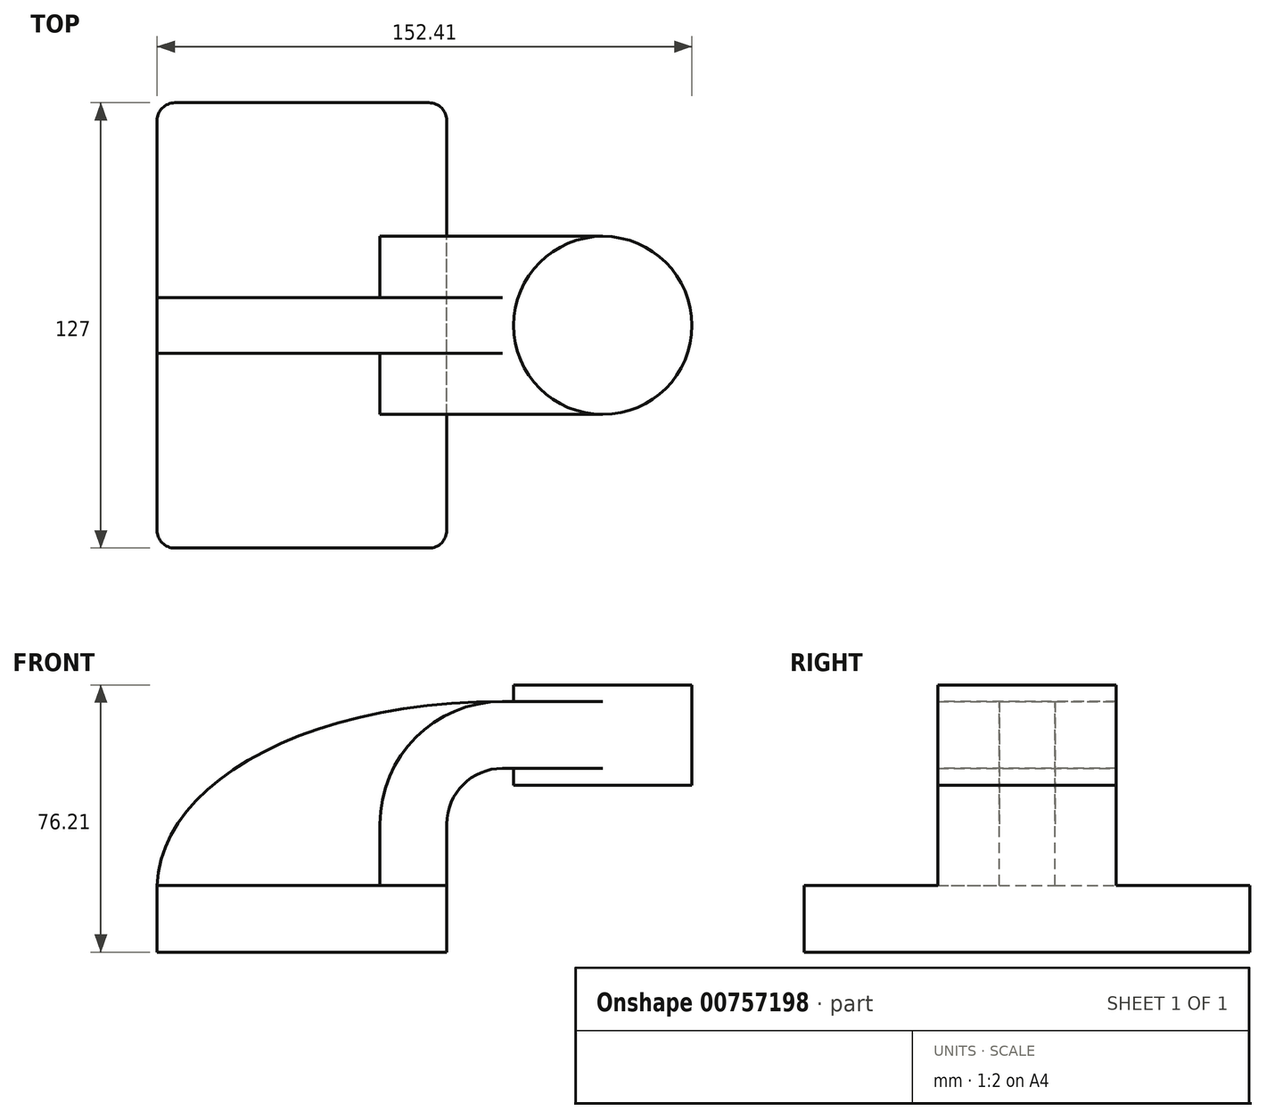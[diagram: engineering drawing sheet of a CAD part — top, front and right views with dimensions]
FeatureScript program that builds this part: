
annotation { "Feature Type Name" : "Feature", "Feature Type Description" : "" }
export const myFeature = defineFeature(function(context is Context, id is Id, definition is map)
    precondition{}
    {
        {
            var Q0;
            Q0=qCreatedBy(makeId("Front.planeOp"),FACE);
            var sketch = newSketch(context, id + "F0", { "sketchPlane" : qUnion([Q0])});
            skLineSegment(sketch, "E0.bottom", {"start": v(41.28, -9.52) * mm, "end": v(-41.28, -9.53) * mm});
            skLineSegment(sketch, "E0.top", {"start": v(41.28, 9.53) * mm, "end": v(-41.28, 9.53) * mm});
            skLineSegment(sketch, "E0.left", {"start": v(41.28, -9.52) * mm, "end": v(41.28, 9.53) * mm});
            skLineSegment(sketch, "E0.right", {"start": v(-41.28, -9.53) * mm, "end": v(-41.28, 9.53) * mm});
            skPoint(sketch, "E0.middle", {"position": v(0, 0) * mm});
            skLineSegment(sketch, "E1.bottom", {"start": v(111.12, 38.1) * mm, "end": v(60.32, 38.1) * mm});
            skLineSegment(sketch, "E1.top", {"start": v(111.12, 66.68) * mm, "end": v(60.32, 66.68) * mm});
            skLineSegment(sketch, "E1.left", {"start": v(111.12, 38.1) * mm, "end": v(111.12, 66.68) * mm});
            skLineSegment(sketch, "E1.right", {"start": v(60.32, 38.1) * mm, "end": v(60.32, 66.68) * mm});
            skPoint(sketch, "E1.middle", {"position": v(85.72, 52.39) * mm});
            skLineSegment(sketch, "E2", {"start": v(41.28, 9.53) * mm, "end": v(41.28, 27) * mm});
            skArc(sketch, "E3", {"start": v(57.15, 42.88) * mm, "mid": v(45.92, 38.23) * mm, "end": v(41.27, 27) * mm});
            skLineSegment(sketch, "E4", {"start": v(57.15, 42.88) * mm, "end": v(85.72, 42.88) * mm});
            skLineSegment(sketch, "E5.0", {"start": v(22.23, 9.53) * mm, "end": v(22.23, 27) * mm});
            skArc(sketch, "E5.1", {"start": v(57.15, 61.93) * mm, "mid": v(32.45, 51.7) * mm, "end": v(22.22, 27) * mm});
            skLineSegment(sketch, "E5.2", {"start": v(57.15, 61.93) * mm, "end": v(85.72, 61.93) * mm});
            skFitSpline(sketch, "E6", {"points": [v(-41.28, 9.53) * mm, v(57.15, 61.93) * mm], "startDerivative": vector(2.73, 85.54) * mm, "endDerivative": vector(171.45, 0.1) * mm});
            skLineSegment(sketch, "E7", {"start": v(85.72, 66.68) * mm, "end": v(85.72, 38.1) * mm});
            skSolve(sketch);
        }
        {
            var Q0;
            Q0=makeQuery(id+"F0.imprint","IMPRINT",FACE,{"disambiguationData":[TD([[makeQuery(id+"F0.imprint","IMPRINT",EDGE,{"derivedFrom":sQuery(id+"F0.wireOp",EDGE,"E0.bottom")}),-1.0]])]});
            var Q1;
            Q1=sQuery(id+"F0.wireOp",EDGE,"E0.top");
            var Q2;
            Q2=sQuery(id+"F0.wireOp",EDGE,"E0.bottom");
            var Q3;
            Q3=sQuery(id+"F0.wireOp",EDGE,"E0.left");
            var Q4;
            Q4=sQuery(id+"F0.wireOp",EDGE,"E0.right");
            var Q5;
            Q5=sQuery(id+"F0.wireOp",EDGE,"E1.bottom");
            var Q6;
            Q6=sQuery(id+"F0.wireOp",EDGE,"E1.top");
            var Q7;
            Q7=sQuery(id+"F0.wireOp",EDGE,"E1.left");
            var Q8;
            Q8=sQuery(id+"F0.wireOp",EDGE,"E1.right");
            var Q9;
            Q9=sQuery(id+"F0.wireOp",EDGE,"E2");
            var Q10;
            Q10=sQuery(id+"F0.wireOp",EDGE,"E3");
            var Q11;
            Q11=sQuery(id+"F0.wireOp",EDGE,"E4");
            var Q12;
            Q12=sQuery(id+"F0.wireOp",EDGE,"E5.0");
            var Q13;
            Q13=sQuery(id+"F0.wireOp",EDGE,"E5.1");
            var Q14;
            Q14=sQuery(id+"F0.wireOp",EDGE,"E5.2");
            var Q15;
            Q15=sQuery(id+"F0.wireOp",EDGE,"EhE2OOWu-g3Lf-cFFT-3C2H-O0PvmW2bhb0I");
            extrude(context, id + "F1", {"entities" : qUnion([Q0]), "surfaceEntities" : qUnion([Q1, Q2, Q3, Q4, Q5, Q6, Q7, Q8, Q9, Q10, Q11, Q12, Q13, Q14, Q15]), "endBound" : BoundingType.SYMMETRIC, "depth" : 127 * mm, "offsetDistance" : 25.4 * mm});
        }
        {
            var Q0;
            {var subQ1=sQuery(id+"F0.wireOp",EDGE,"E2");Q0=makeQuery(id+"F0.imprint","IMPRINT",FACE,{"disambiguationData":[TD([[makeQuery(id+"F0.imprint","IMPRINT",EDGE,{"derivedFrom":subQ1}),1.0]])]});}
            var Q1;
            {var subQ0=sQuery(id+"F0.wireOp",EDGE,"E4");var subQ1=sQuery(id+"F0.wireOp",EDGE,"E1.right");var subQ2=makeQuery(id+"F0.imprint","INTERSECT",VERTEX,{"derivedFrom":[subQ1,subQ0]});Q1=makeQuery(id+"F0.imprint","IMPRINT",FACE,{"disambiguationData":[TD([[makeQuery(id+"F0.imprint","IMPRINT",EDGE,{"disambiguationData":[TD([[subQ2,-1.0]])],"derivedFrom":subQ1}),-1.0]])]});}
            extrude(context, id + "F2", {"entities" : qUnion([Q0, Q1]), "operationType" : NewBodyOperationType.ADD, "endBound" : BoundingType.SYMMETRIC, "depth" : 50.8 * mm, "offsetDistance" : 25.4 * mm});
        }
        {
            var Q0;
            Q0=makeQuery(id+"F0.imprint","IMPRINT",FACE,{"disambiguationData":[TD([[makeQuery(id+"F0.imprint","IMPRINT",EDGE,{"derivedFrom":sQuery(id+"F0.wireOp",EDGE,"E0.bottom")}),-1.0]])]});
            var Q1;
            {var subQ1=sQuery(id+"F0.wireOp",EDGE,"E2");Q1=makeQuery(id+"F0.imprint","IMPRINT",FACE,{"disambiguationData":[TD([[makeQuery(id+"F0.imprint","IMPRINT",EDGE,{"derivedFrom":subQ1}),1.0]])]});}
            var Q2;
            {var subQ2=sQuery(id+"F0.wireOp",EDGE,"E5.0");Q2=makeQuery(id+"F0.imprint","IMPRINT",FACE,{"disambiguationData":[TD([[makeQuery(id+"F0.imprint","IMPRINT",EDGE,{"derivedFrom":subQ2}),1.0]])]});}
            extrude(context, id + "F3", {"entities" : qUnion([Q0, Q1, Q2]), "operationType" : NewBodyOperationType.ADD, "endBound" : BoundingType.SYMMETRIC, "depth" : 15.88 * mm, "offsetDistance" : 25.4 * mm});
        }
        {
            var Q0;
            {var subQ4=sQuery(id+"F0.wireOp",EDGE,"E1.left");Q0=makeQuery(id+"F0.imprint","IMPRINT",FACE,{"disambiguationData":[TD([[makeQuery(id+"F0.imprint","IMPRINT",EDGE,{"derivedFrom":subQ4}),1.0]])]});}
            var Q1;
            Q1=sQuery(id+"F0.wireOp",EDGE,"E7");
            revolve(context, id + "F4", {"operationType" : NewBodyOperationType.ADD, "surfaceOperationType" : NewSurfaceOperationType.NEW, "entities" : qUnion([Q0]), "axis" : qUnion([Q1]), "revolveType" : RevolveType.FULL});
        }
        {
            var Q0;
            Q0=makeQuery(id+"F1.opExtrude","CAP_EDGE",EDGE,{"disambiguationData":[OSD([sQuery(id+"F0.wireOp",EDGE,"E0.right")])],"isStart":false});
            var Q1;
            Q1=makeQuery(id+"F1.opExtrude","CAP_EDGE",EDGE,{"disambiguationData":[OSD([sQuery(id+"F0.wireOp",EDGE,"E0.left")])],"isStart":false});
            var Q2;
            Q2=makeQuery(id+"F1.opExtrude","CAP_EDGE",EDGE,{"disambiguationData":[OSD([sQuery(id+"F0.wireOp",EDGE,"E0.left")])],"isStart":true});
            var Q3;
            Q3=makeQuery(id+"F1.opExtrude","CAP_EDGE",EDGE,{"disambiguationData":[OSD([sQuery(id+"F0.wireOp",EDGE,"E0.right")])],"isStart":true});
            fillet(context, id + "F5", {"entities" : qUnion([Q0, Q1, Q2, Q3]), "radius" : 5.08 * mm, "tangentPropagation" : true, "allowEdgeOverflow" : false});
        }
    });
